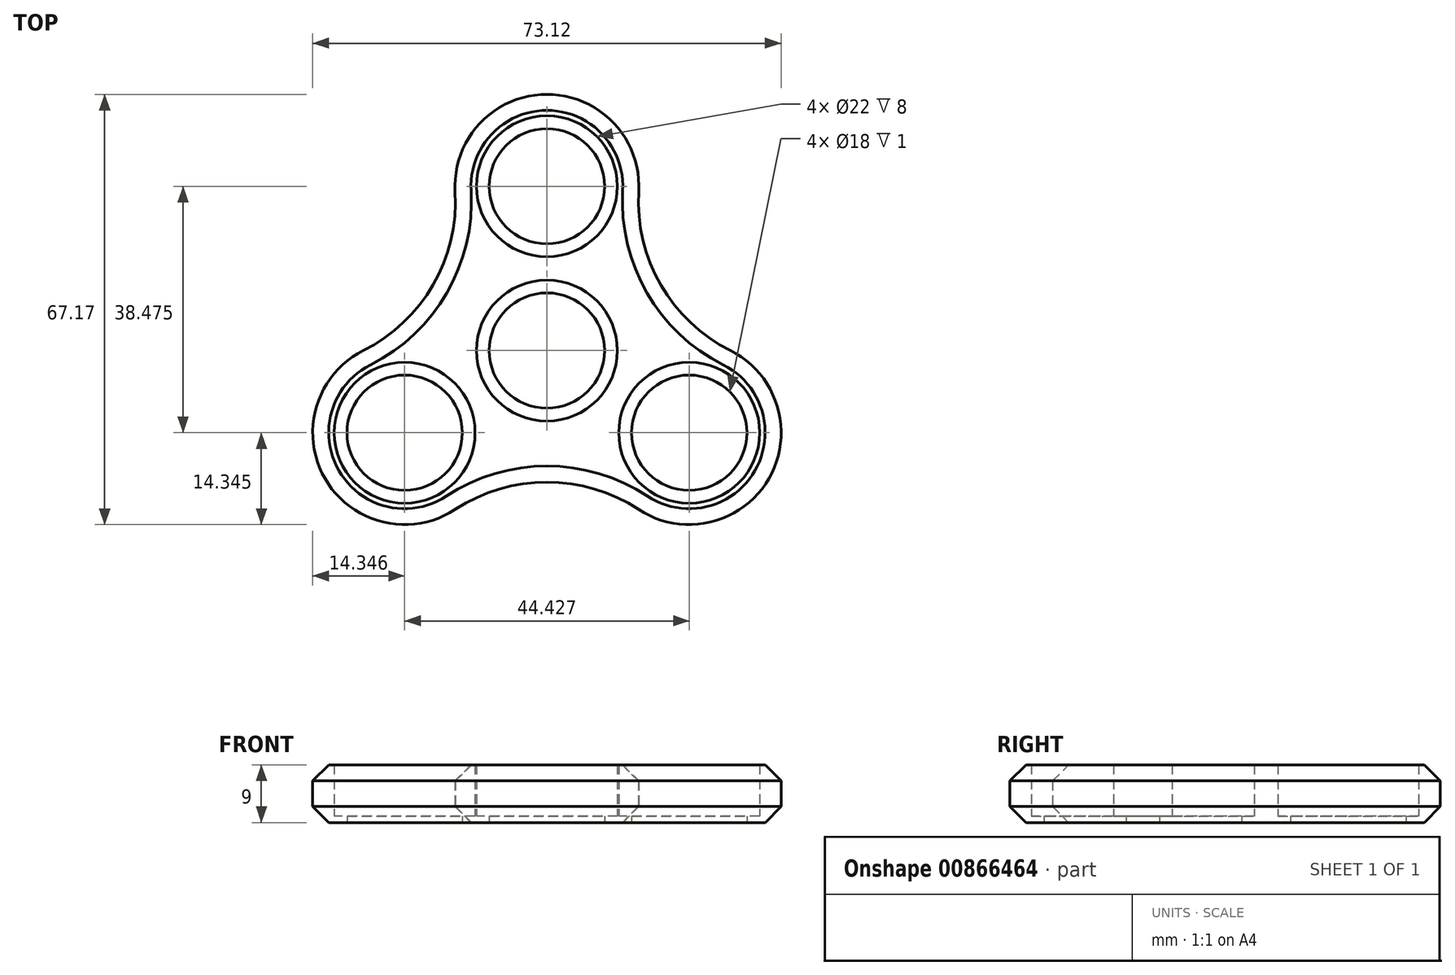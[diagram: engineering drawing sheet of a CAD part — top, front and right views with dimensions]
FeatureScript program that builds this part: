
annotation { "Feature Type Name" : "Feature", "Feature Type Description" : "" }
export const myFeature = defineFeature(function(context is Context, id is Id, definition is map)
    precondition{}
    {
        {
            var Q0;
            Q0=qCreatedBy(makeId("Top.planeOp"),FACE);
            var sketch = newSketch(context, id + "F0", { "sketchPlane" : qUnion([Q0])});
            skCircle(sketch, "E0", {"center": v(0, 0) * mm, "radius": 40 * mm, "construction": true});
            skCircle(sketch, "E1", {"center": v(0, 0) * mm, "radius": 11 * mm});
            skCircle(sketch, "E2", {"center": v(0, 25.65) * mm, "radius": 14.35 * mm});
            skCircle(sketch, "E3", {"center": v(0, 25.65) * mm, "radius": 11 * mm});
            skCircle(sketch, "E4.1.0", {"center": v(-22.21, -12.83) * mm, "radius": 11 * mm});
            skCircle(sketch, "E4.1.1", {"center": v(-22.21, -12.83) * mm, "radius": 14.35 * mm});
            skCircle(sketch, "E4.2.0", {"center": v(22.21, -12.83) * mm, "radius": 11 * mm});
            skCircle(sketch, "E4.2.1", {"center": v(22.21, -12.83) * mm, "radius": 14.35 * mm});
            skLineSegment(sketch, "E5", {"start": v(0, 0) * mm, "end": v(0, 58.53) * mm, "construction": true});
            skLineSegment(sketch, "E6", {"start": v(0, 0) * mm, "end": v(-53.01, 30.6) * mm, "construction": true});
            skArc(sketch, "E7", {"start": v(-28.65, 0) * mm, "mid": v(-17.77, 10.26) * mm, "end": v(-14.33, 24.81) * mm});
            skLineSegment(sketch, "E8", {"start": v(0, 0) * mm, "end": v(22.21, -12.83) * mm, "construction": true});
            skArc(sketch, "E9.1.0", {"start": v(14.33, -24.81) * mm, "mid": v(0, -20.52) * mm, "end": v(-14.33, -24.81) * mm});
            skArc(sketch, "E9.2.0", {"start": v(14.33, 24.81) * mm, "mid": v(17.77, 10.26) * mm, "end": v(28.65, 0) * mm});
            skLineSegment(sketch, "E10", {"start": v(0, 0) * mm, "end": v(-22.21, -12.83) * mm, "construction": true});
            skSolve(sketch);
        }
        {
            var Q0;
            Q0 = qSketchRegion(id + "F0", true);
            extrude(context, id + "F1", {"entities" : qUnion([Q0]), "depth" : 9 * mm, "offsetDistance" : 25 * mm});
        }
        {
            var Q0;
            Q0=makeQuery(id+"F1.opExtrude","CAP_EDGE",EDGE,{"disambiguationData":[OSD([sQuery(id+"F0.wireOp",EDGE,"E9.2.0")])],"isStart":false});
            var Q1;
            Q1=makeQuery(id+"F1.opExtrude","CAP_EDGE",EDGE,{"disambiguationData":[OSD([sQuery(id+"F0.wireOp",EDGE,"E9.2.0")])],"isStart":true});
            chamfer(context, id + "F2", {"entities" : qUnion([Q0, Q1]), "width" : 2.5 * mm, "tangentPropagation" : true});
        }
        {
            var Q0;
            Q0=makeQuery(id+"F1.opExtrude","CAP_FACE",FACE,{"disambiguationData":[OSD([sQuery(id+"F0.wireOp",EDGE,"E1"),sQuery(id+"F0.wireOp",EDGE,"E2"),sQuery(id+"F0.wireOp",EDGE,"E3"),sQuery(id+"F0.wireOp",EDGE,"E4.1.0"),sQuery(id+"F0.wireOp",EDGE,"E4.1.1"),sQuery(id+"F0.wireOp",EDGE,"E4.2.0"),sQuery(id+"F0.wireOp",EDGE,"E4.2.1"),sQuery(id+"F0.wireOp",EDGE,"E7"),sQuery(id+"F0.wireOp",EDGE,"E9.1.0"),sQuery(id+"F0.wireOp",EDGE,"E9.2.0")])],"isStart":true});
            var sketch = newSketch(context, id + "F3", { "sketchPlane" : qUnion([Q0])});
            skCircle(sketch, "E11.0", {"center": v(22.21, 12.83) * mm, "radius": 11 * mm});
            skCircle(sketch, "E12.0", {"center": v(-22.21, 12.83) * mm, "radius": 11 * mm});
            skCircle(sketch, "E13.0", {"center": v(0, 0) * mm, "radius": 11 * mm});
            skCircle(sketch, "E14.0", {"center": v(0, -25.65) * mm, "radius": 11 * mm});
            skCircle(sketch, "E15", {"center": v(-22.21, 12.83) * mm, "radius": 9 * mm});
            skCircle(sketch, "E16", {"center": v(0, 0) * mm, "radius": 9 * mm});
            skCircle(sketch, "E17", {"center": v(22.21, 12.83) * mm, "radius": 9 * mm});
            skCircle(sketch, "E18", {"center": v(0, -25.65) * mm, "radius": 9 * mm});
            skSolve(sketch);
        }
        {
            var Q0;
            Q0 = qSketchRegion(id + "F3", true);
            extrude(context, id + "F4", {"entities" : qUnion([Q0]), "operationType" : NewBodyOperationType.ADD, "oppositeDirection" : true, "depth" : 1 * mm, "offsetDistance" : 25 * mm});
        }
    });
